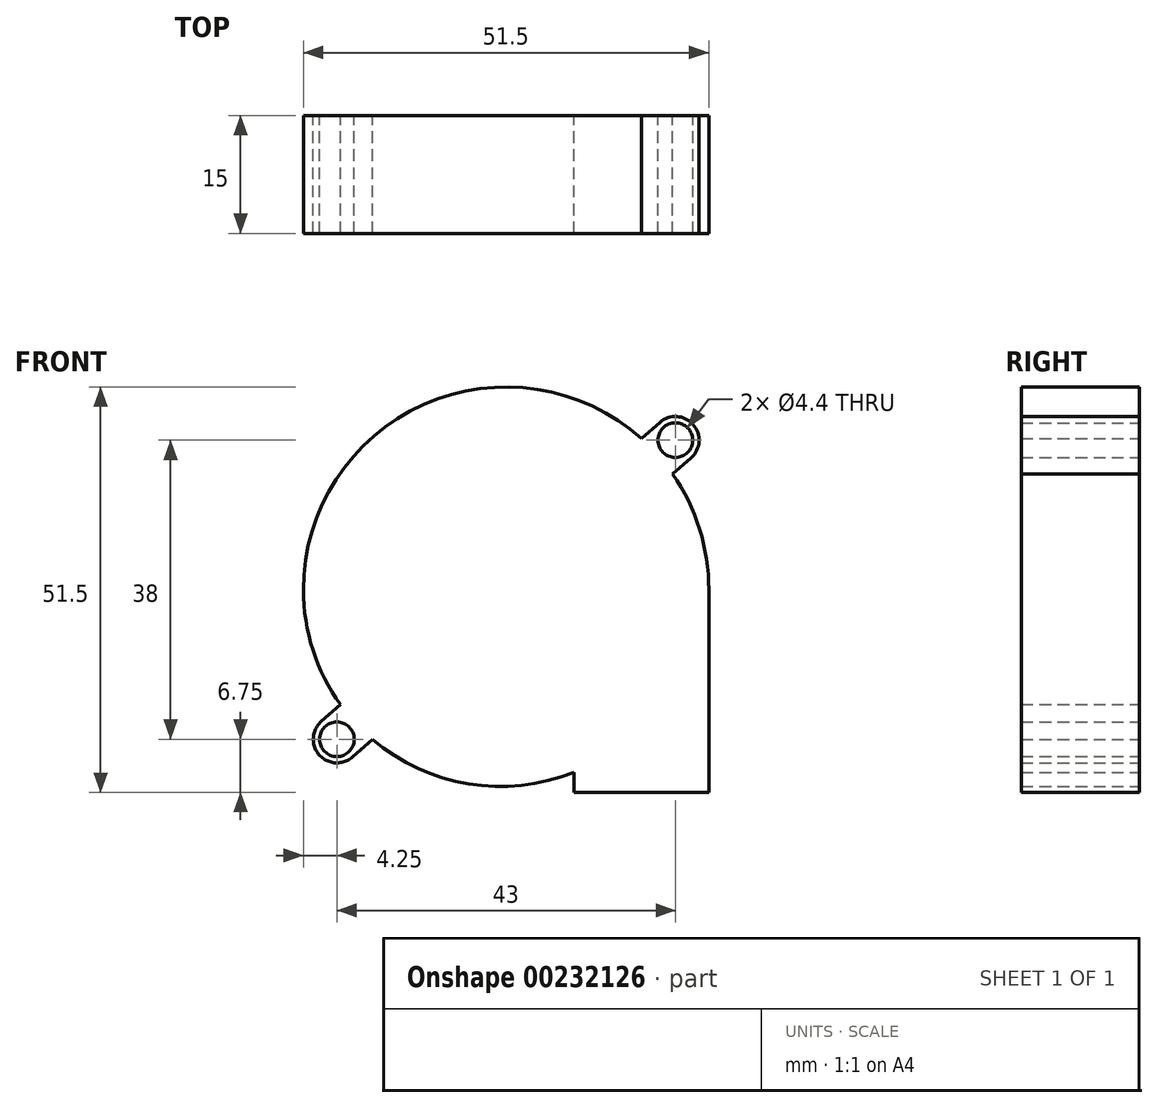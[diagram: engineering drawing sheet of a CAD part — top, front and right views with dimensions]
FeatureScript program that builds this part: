
annotation { "Feature Type Name" : "Feature", "Feature Type Description" : "" }
export const myFeature = defineFeature(function(context is Context, id is Id, definition is map)
    precondition{}
    {
        {
            var Q0;
            Q0=qCreatedBy(makeId("Front.planeOp"),FACE);
            var sketch = newSketch(context, id + "F0", { "sketchPlane" : qUnion([Q0])});
            skLineSegment(sketch, "E0.top", {"start": v(25.75, -25.75) * mm, "end": v(8.6, -25.75) * mm});
            skLineSegment(sketch, "E0.left", {"start": v(25.75, 0) * mm, "end": v(25.75, -25.75) * mm});
            skPoint(sketch, "E0.middle", {"position": v(0, 0) * mm});
            skArc(sketch, "E1", {"start": v(25.75, 0) * mm, "mid": v(24.57, 7.7) * mm, "end": v(21.15, 14.69) * mm});
            skArc(sketch, "E2", {"start": v(-25.75, 0) * mm, "mid": v(-24.55, -7.67) * mm, "end": v(-21.05, -14.6) * mm});
            skLineSegment(sketch, "E3", {"start": v(8.6, -25.75) * mm, "end": v(8.6, -23.19) * mm});
            skCircle(sketch, "E4", {"center": v(21.5, 19) * mm, "radius": 2.2 * mm});
            skCircle(sketch, "E5", {"center": v(-21.5, -19) * mm, "radius": 2.2 * mm});
            skArc(sketch, "E6", {"start": v(-23.49, -16.75) * mm, "mid": v(-23.75, -20.99) * mm, "end": v(-19.51, -21.25) * mm});
            skArc(sketch, "E7", {"start": v(23.49, 16.75) * mm, "mid": v(23.75, 20.99) * mm, "end": v(19.51, 21.25) * mm});
            skLineSegment(sketch, "E8", {"start": v(-23.49, -16.75) * mm, "end": v(-21.05, -14.6) * mm});
            skLineSegment(sketch, "E9", {"start": v(-19.51, -21.25) * mm, "end": v(-16.98, -19.01) * mm});
            skLineSegment(sketch, "E10", {"start": v(-21.5, -19) * mm, "end": v(21.5, 19) * mm, "construction": true});
            skArc(sketch, "E11.trimOffspring", {"start": v(-16.98, -19.01) * mm, "mid": v(-4.78, -24.67) * mm, "end": v(8.6, -23.19) * mm});
            skLineSegment(sketch, "E12", {"start": v(19.51, 21.25) * mm, "end": v(17.18, 19.18) * mm});
            skLineSegment(sketch, "E13", {"start": v(23.49, 16.75) * mm, "end": v(21.15, 14.69) * mm});
            skArc(sketch, "E14.trimOffspring", {"start": v(17.18, 19.18) * mm, "mid": v(-10.5, 23.5) * mm, "end": v(-25.75, 0) * mm});
            skSolve(sketch);
        }
        {
            var Q0;
            Q0=makeQuery(id+"F0.imprint","IMPRINT",FACE,{"disambiguationData":[TD([[makeQuery(id+"F0.imprint","IMPRINT",EDGE,{"derivedFrom":sQuery(id+"F0.wireOp",EDGE,"E0.top")}),-1.0]])]});
            extrude(context, id + "F1", {"entities" : qUnion([Q0]), "depth" : 15 * mm});
        }
    });
